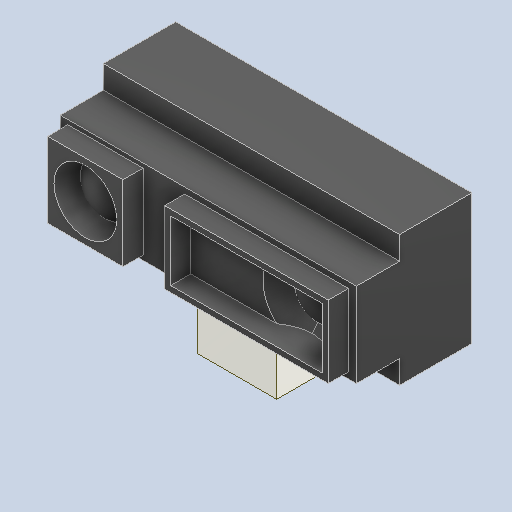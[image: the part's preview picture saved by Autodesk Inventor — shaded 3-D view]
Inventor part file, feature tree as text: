
AUTODESK INVENTOR PART (.ipt)
format: ipt  version: 2023 (Build 270158000, 158)  size: 384,000 bytes
history: native  units: in
note: dims shown in document units (in); Inventor stores cm internally (conversion verified against a paired STEP export)
features: other x10, extrude x1, sketch x1, projected_geometry x1
ambient origin geometry x8: Origin, YZ Plane, XZ Plane, XY Plane, X Axis, Y Axis, Z Axis, Center Point
bodies: Body1 (feature_tree), Body2 (feature_tree), Body3 (feature_tree), Body4 (feature_tree), Body5 (feature_tree)
feature tree (13):
  other  "Bryła1"
  extrude  "Wyciągnięcie proste1"  TaperAngle=0.0deg  [1 undecoded]
  other  "Bryła2"
  other  "Bryła3"
  other  "Bryła4"
  other  "Bryła5"
  sketch  "Szkic1"
  projected_geometry  "Pętla rzutowana1"
  other  "Sensor"
  other  "Light_Detector"
  other  "Light_Emitter"
  other  "Connector"
  other  "PCB"
note: 1 required parameter value undecoded (feature->parameter linkage not recoverable at this tier; creation-order binding heuristic only, values carry confidence <= 0.55)
